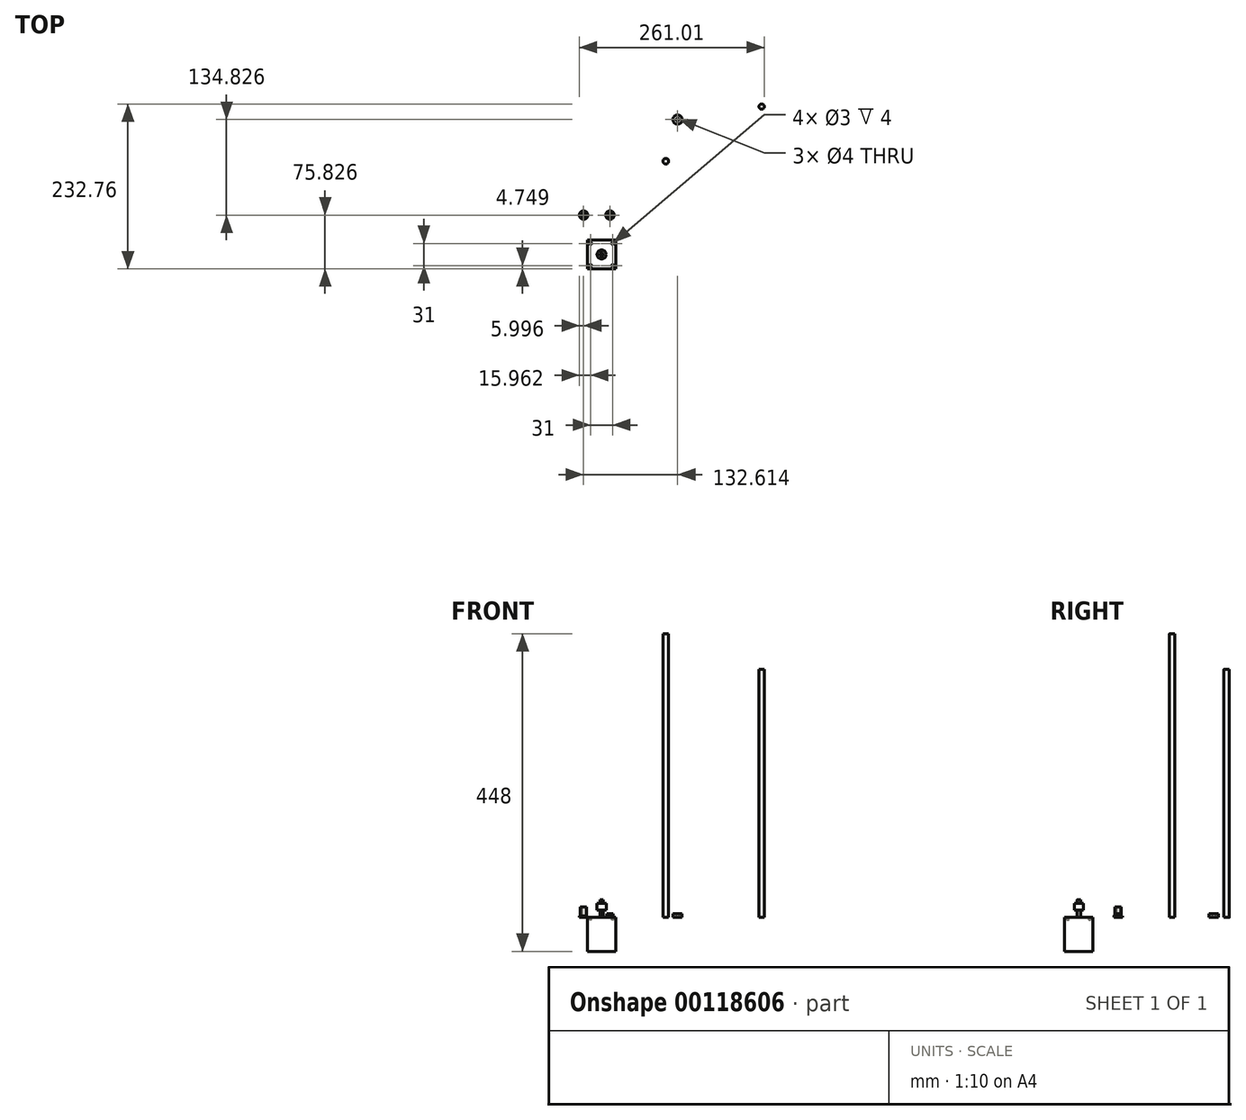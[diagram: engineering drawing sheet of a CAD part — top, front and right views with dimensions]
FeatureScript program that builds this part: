
annotation { "Feature Type Name" : "Feature", "Feature Type Description" : "" }
export const myFeature = defineFeature(function(context is Context, id is Id, definition is map)
    precondition{}
    {
        {
            var Q0;
            Q0=qCreatedBy(makeId("Top.planeOp"),FACE);
            var sketch = newSketch(context, id + "F0", { "sketchPlane" : qUnion([Q0])});
            skCircle(sketch, "E0", {"center": v(-93.77, -34.85) * mm, "radius": 4 * mm});
            skCircle(sketch, "E1", {"center": v(-77.16, 23.93) * mm, "radius": 2 * mm});
            skCircle(sketch, "E2", {"center": v(-77.16, 23.93) * mm, "radius": 6.5 * mm});
            skCircle(sketch, "E3", {"center": v(-209.77, -110.9) * mm, "radius": 6 * mm});
            skCircle(sketch, "E4", {"center": v(-209.77, -110.9) * mm, "radius": 4.5 * mm});
            skCircle(sketch, "E5", {"center": v(-209.77, -110.9) * mm, "radius": 2 * mm});
            skCircle(sketch, "E6", {"center": v(-172.5, -110.9) * mm, "radius": 2 * mm});
            skCircle(sketch, "E7", {"center": v(-172.5, -110.9) * mm, "radius": 4.5 * mm});
            skCircle(sketch, "E8", {"center": v(-172.5, -110.9) * mm, "radius": 6 * mm});
            skSolve(sketch);
        }
        {
            var Q0;
            Q0=makeQuery(id+"F0.imprint","IMPRINT",FACE,{"disambiguationData":[TD([[makeQuery(id+"F0.imprint","IMPRINT",EDGE,{"derivedFrom":sQuery(id+"F0.wireOp",EDGE,"E0")}),1.0]])]});
            extrude(context, id + "F1", {"entities" : qUnion([Q0]), "depth" : 400 * mm});
        }
        {
            var Q0;
            Q0=makeQuery(id+"F0.imprint","IMPRINT",FACE,{"disambiguationData":[TD([[makeQuery(id+"F0.imprint","IMPRINT",EDGE,{"derivedFrom":sQuery(id+"F0.wireOp",EDGE,"E1")}),-1.0]])]});
            extrude(context, id + "F2", {"entities" : qUnion([Q0]), "depth" : 5 * mm});
        }
        {
            var Q0;
            Q0=qCreatedBy(makeId("Top.planeOp"),FACE);
            var sketch = newSketch(context, id + "F3", { "sketchPlane" : qUnion([Q0])});
            skLineSegment(sketch, "E9.bottom", {"start": v(-164.06, -186.72) * mm, "end": v(-204.56, -186.72) * mm});
            skLineSegment(sketch, "E9.top", {"start": v(-164.06, -146.22) * mm, "end": v(-204.56, -146.22) * mm});
            skLineSegment(sketch, "E9.left", {"start": v(-164.06, -186.72) * mm, "end": v(-164.06, -146.22) * mm});
            skLineSegment(sketch, "E9.right", {"start": v(-204.56, -186.72) * mm, "end": v(-204.56, -146.22) * mm});
            skLineSegment(sketch, "E10", {"start": v(-184.3, -146.22) * mm, "end": v(-184.3, -186.72) * mm, "construction": true});
            skCircle(sketch, "E11", {"center": v(-184.3, -166.47) * mm, "radius": 2.5 * mm});
            skCircle(sketch, "E12", {"center": v(-184.3, -166.47) * mm, "radius": 6.37 * mm});
            skCircle(sketch, "E13", {"center": v(-199.8, -150.97) * mm, "radius": 1.5 * mm});
            skCircle(sketch, "E14", {"center": v(-168.8, -150.97) * mm, "radius": 1.5 * mm});
            skCircle(sketch, "E15", {"center": v(-168.8, -181.97) * mm, "radius": 1.5 * mm});
            skCircle(sketch, "E16", {"center": v(-199.8, -181.97) * mm, "radius": 1.5 * mm});
            skLineSegment(sketch, "E17", {"start": v(-199.8, -150.97) * mm, "end": v(-204.56, -150.97) * mm, "construction": true});
            skLineSegment(sketch, "E18", {"start": v(-199.8, -150.97) * mm, "end": v(-199.8, -146.22) * mm, "construction": true});
            skLineSegment(sketch, "E19", {"start": v(-199.8, -181.97) * mm, "end": v(-199.8, -186.72) * mm, "construction": true});
            skLineSegment(sketch, "E20", {"start": v(-199.8, -181.97) * mm, "end": v(-204.56, -181.97) * mm, "construction": true});
            skLineSegment(sketch, "E21", {"start": v(-168.8, -150.97) * mm, "end": v(-168.8, -146.22) * mm, "construction": true});
            skLineSegment(sketch, "E22", {"start": v(-168.8, -150.97) * mm, "end": v(-164.06, -150.97) * mm, "construction": true});
            skLineSegment(sketch, "E23", {"start": v(-168.8, -181.97) * mm, "end": v(-164.06, -181.97) * mm, "construction": true});
            skLineSegment(sketch, "E24", {"start": v(-168.8, -181.97) * mm, "end": v(-168.8, -186.72) * mm, "construction": true});
            skSolve(sketch);
        }
        {
            var Q0;
            Q0=makeQuery(id+"F3.imprint","IMPRINT",FACE,{"disambiguationData":[TD([[makeQuery(id+"F3.imprint","IMPRINT",EDGE,{"derivedFrom":sQuery(id+"F3.wireOp",EDGE,"E9.bottom")}),-1.0]])]});
            var Q1;
            Q1=makeQuery(id+"F3.imprint","IMPRINT",FACE,{"disambiguationData":[TD([[makeQuery(id+"F3.imprint","IMPRINT",EDGE,{"derivedFrom":sQuery(id+"F3.wireOp",EDGE,"E16")}),1.0]])]});
            var Q2;
            Q2=makeQuery(id+"F3.imprint","IMPRINT",FACE,{"disambiguationData":[TD([[makeQuery(id+"F3.imprint","IMPRINT",EDGE,{"derivedFrom":sQuery(id+"F3.wireOp",EDGE,"E11")}),1.0]])]});
            var Q3;
            Q3=makeQuery(id+"F3.imprint","IMPRINT",FACE,{"disambiguationData":[TD([[makeQuery(id+"F3.imprint","IMPRINT",EDGE,{"derivedFrom":sQuery(id+"F3.wireOp",EDGE,"E11")}),-1.0]])]});
            var Q4;
            Q4=makeQuery(id+"F3.imprint","IMPRINT",FACE,{"disambiguationData":[TD([[makeQuery(id+"F3.imprint","IMPRINT",EDGE,{"derivedFrom":sQuery(id+"F3.wireOp",EDGE,"E13")}),1.0]])]});
            var Q5;
            Q5=makeQuery(id+"F3.imprint","IMPRINT",FACE,{"disambiguationData":[TD([[makeQuery(id+"F3.imprint","IMPRINT",EDGE,{"derivedFrom":sQuery(id+"F3.wireOp",EDGE,"E14")}),1.0]])]});
            var Q6;
            Q6=makeQuery(id+"F3.imprint","IMPRINT",FACE,{"disambiguationData":[TD([[makeQuery(id+"F3.imprint","IMPRINT",EDGE,{"derivedFrom":sQuery(id+"F3.wireOp",EDGE,"E15")}),1.0]])]});
            extrude(context, id + "F4", {"entities" : qUnion([Q0, Q1, Q2, Q3, Q4, Q5, Q6]), "oppositeDirection" : true, "depth" : 48 * mm});
        }
        {
            var Q0;
            Q0=makeQuery(id+"F3.imprint","IMPRINT",FACE,{"disambiguationData":[TD([[makeQuery(id+"F3.imprint","IMPRINT",EDGE,{"derivedFrom":sQuery(id+"F3.wireOp",EDGE,"E13")}),1.0]])]});
            var Q1;
            Q1=makeQuery(id+"F3.imprint","IMPRINT",FACE,{"disambiguationData":[TD([[makeQuery(id+"F3.imprint","IMPRINT",EDGE,{"derivedFrom":sQuery(id+"F3.wireOp",EDGE,"E16")}),1.0]])]});
            var Q2;
            Q2=makeQuery(id+"F3.imprint","IMPRINT",FACE,{"disambiguationData":[TD([[makeQuery(id+"F3.imprint","IMPRINT",EDGE,{"derivedFrom":sQuery(id+"F3.wireOp",EDGE,"E15")}),1.0]])]});
            var Q3;
            Q3=makeQuery(id+"F3.imprint","IMPRINT",FACE,{"disambiguationData":[TD([[makeQuery(id+"F3.imprint","IMPRINT",EDGE,{"derivedFrom":sQuery(id+"F3.wireOp",EDGE,"E14")}),1.0]])]});
            extrude(context, id + "F5", {"entities" : qUnion([Q0, Q1, Q2, Q3]), "operationType" : NewBodyOperationType.REMOVE, "oppositeDirection" : true, "depth" : 4 * mm});
        }
        {
            var Q0;
            Q0=makeQuery(id+"F3.imprint","IMPRINT",FACE,{"disambiguationData":[TD([[makeQuery(id+"F3.imprint","IMPRINT",EDGE,{"derivedFrom":sQuery(id+"F3.wireOp",EDGE,"E11")}),1.0]])]});
            extrude(context, id + "F6", {"entities" : qUnion([Q0]), "operationType" : NewBodyOperationType.ADD, "depth" : 24.5 * mm});
        }
        {
            var Q0;
            Q0=makeQuery(id+"F3.imprint","IMPRINT",FACE,{"disambiguationData":[TD([[makeQuery(id+"F3.imprint","IMPRINT",EDGE,{"derivedFrom":sQuery(id+"F3.wireOp",EDGE,"E11")}),-1.0]])]});
            extrude(context, id + "F7", {"entities" : qUnion([Q0]), "operationType" : NewBodyOperationType.ADD, "depth" : 20 * mm, "hasSecondDirection" : true, "secondDirectionOppositeDirection" : false, "secondDirectionDepth" : 10 * mm});
        }
        {
            var Q0;
            Q0=qCreatedBy(makeId("Top.planeOp"),FACE);
            var sketch = newSketch(context, id + "F8", { "sketchPlane" : qUnion([Q0])});
            skCircle(sketch, "E25", {"center": v(41.5, 42.29) * mm, "radius": 3.75 * mm});
            skSolve(sketch);
        }
        {
            var Q0;
            Q0=makeQuery(id+"F8.imprint","IMPRINT",FACE,{"disambiguationData":[TD([[makeQuery(id+"F8.imprint","IMPRINT",EDGE,{"derivedFrom":sQuery(id+"F8.wireOp",EDGE,"E25")}),1.0]])]});
            extrude(context, id + "F9", {"entities" : qUnion([Q0]), "depth" : 350 * mm});
        }
        {
            var Q0;
            Q0=makeQuery(id+"F0.imprint","IMPRINT",FACE,{"disambiguationData":[TD([[makeQuery(id+"F0.imprint","IMPRINT",EDGE,{"derivedFrom":sQuery(id+"F0.wireOp",EDGE,"E4")}),1.0]])]});
            var Q1;
            Q1=makeQuery(id+"F0.imprint","IMPRINT",FACE,{"disambiguationData":[TD([[makeQuery(id+"F0.imprint","IMPRINT",EDGE,{"derivedFrom":sQuery(id+"F0.wireOp",EDGE,"E3")}),1.0]])]});
            var Q2;
            Q2=makeQuery(id+"F0.imprint","IMPRINT",FACE,{"disambiguationData":[TD([[makeQuery(id+"F0.imprint","IMPRINT",EDGE,{"derivedFrom":sQuery(id+"F0.wireOp",EDGE,"E6")}),-1.0]])]});
            var Q3;
            Q3=makeQuery(id+"F0.imprint","IMPRINT",FACE,{"disambiguationData":[TD([[makeQuery(id+"F0.imprint","IMPRINT",EDGE,{"derivedFrom":sQuery(id+"F0.wireOp",EDGE,"E7")}),-1.0]])]});
            extrude(context, id + "F10", {"entities" : qUnion([Q0, Q1, Q2, Q3]), "depth" : 2 * mm, "offsetDistance" : 25 * mm});
        }
        {
            var Q0;
            Q0=makeQuery(id+"F0.imprint","IMPRINT",FACE,{"disambiguationData":[TD([[makeQuery(id+"F0.imprint","IMPRINT",EDGE,{"derivedFrom":sQuery(id+"F0.wireOp",EDGE,"E4")}),1.0]])]});
            extrude(context, id + "F11", {"entities" : qUnion([Q0]), "operationType" : NewBodyOperationType.ADD, "depth" : 14.5 * mm, "offsetDistance" : 25 * mm});
        }
        {
            var Q0;
            Q0=makeQuery(id+"F0.imprint","IMPRINT",FACE,{"disambiguationData":[TD([[makeQuery(id+"F0.imprint","IMPRINT",EDGE,{"derivedFrom":sQuery(id+"F0.wireOp",EDGE,"E6")}),-1.0]])]});
            extrude(context, id + "F12", {"entities" : qUnion([Q0]), "operationType" : NewBodyOperationType.ADD, "depth" : 5 * mm, "offsetDistance" : 25 * mm});
        }
    });
